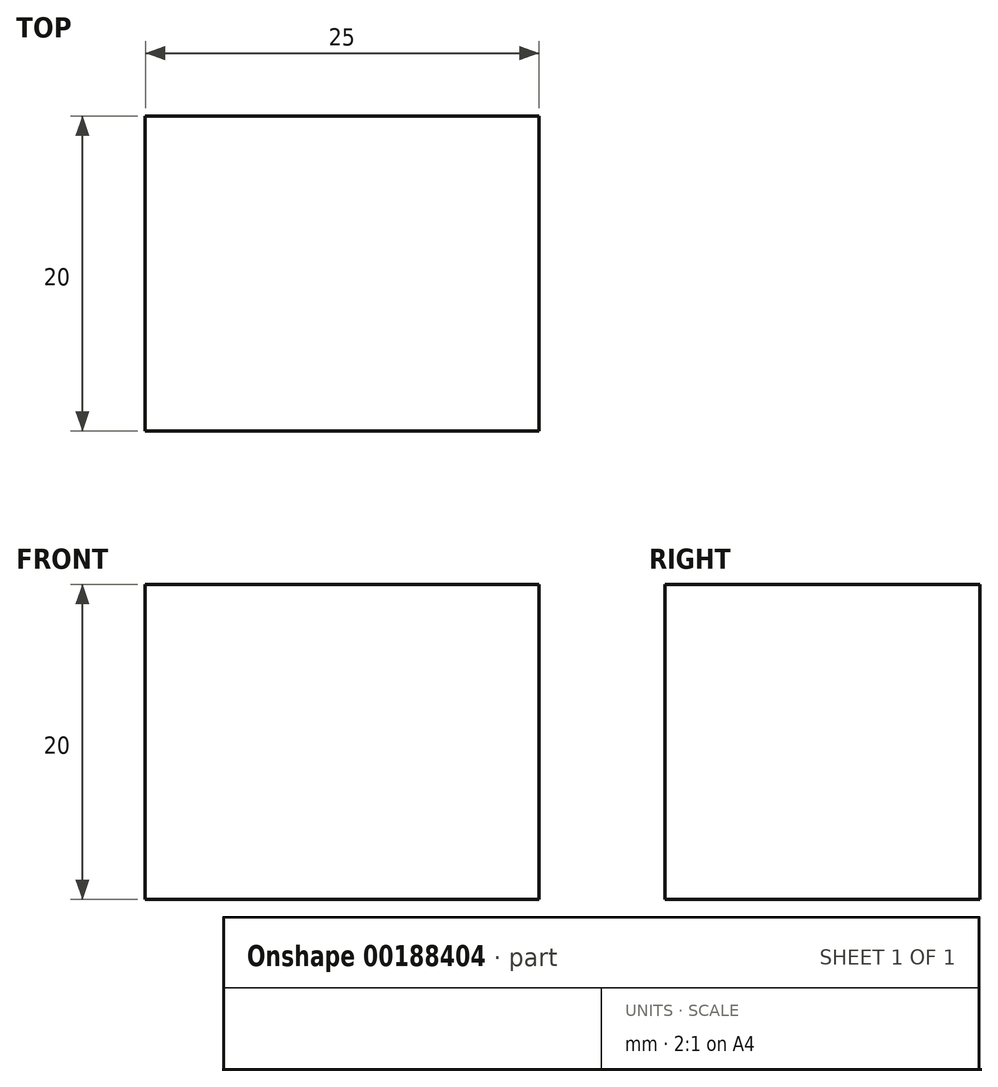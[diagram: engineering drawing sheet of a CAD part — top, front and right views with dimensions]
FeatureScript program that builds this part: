
annotation { "Feature Type Name" : "Feature", "Feature Type Description" : "" }
export const myFeature = defineFeature(function(context is Context, id is Id, definition is map)
    precondition{}
    {
        {
            var Q0;
            Q0=qCreatedBy(makeId("Top.planeOp"),FACE);
            var sketch = newSketch(context, id + "F0", { "sketchPlane" : qUnion([Q0])});
            skLineSegment(sketch, "E0.bottom", {"start": v(-469.08, -14.45) * mm, "end": v(-444.08, -14.45) * mm});
            skLineSegment(sketch, "E0.top", {"start": v(-469.08, -34.45) * mm, "end": v(-444.08, -34.45) * mm});
            skLineSegment(sketch, "E0.left", {"start": v(-469.08, -14.45) * mm, "end": v(-469.08, -34.45) * mm});
            skLineSegment(sketch, "E0.right", {"start": v(-444.08, -14.45) * mm, "end": v(-444.08, -34.45) * mm});
            skSolve(sketch);
        }
        {
            var Q0;
            Q0=makeQuery(id+"F0.imprint","IMPRINT",FACE,{"disambiguationData":[TD([[makeQuery(id+"F0.imprint","IMPRINT",EDGE,{"derivedFrom":sQuery(id+"F0.wireOp",EDGE,"E0.bottom")}),-1.0]])]});
            extrude(context, id + "F1", {"entities" : qUnion([Q0]), "depth" : 20 * mm});
        }
    });
